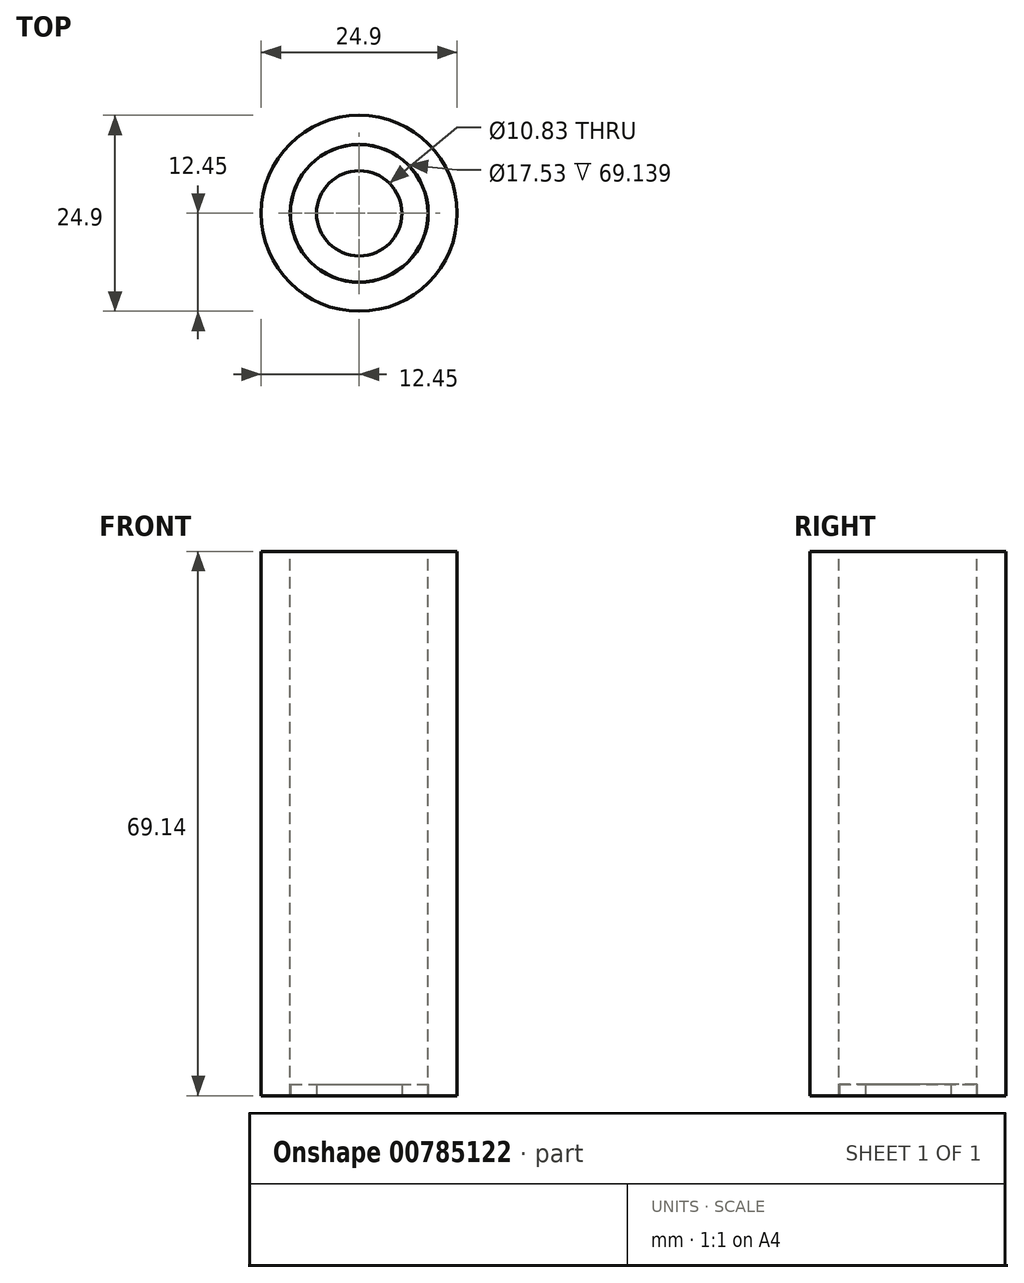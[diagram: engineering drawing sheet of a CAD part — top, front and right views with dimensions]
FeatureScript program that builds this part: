
annotation { "Feature Type Name" : "Feature", "Feature Type Description" : "" }
export const myFeature = defineFeature(function(context is Context, id is Id, definition is map)
    precondition{}
    {
        {
            var Q0;
            Q0=qCreatedBy(makeId("Top.planeOp"),FACE);
            var sketch = newSketch(context, id + "F0", { "sketchPlane" : qUnion([Q0])});
            skCircle(sketch, "E0", {"center": v(0, 0) * mm, "radius": 12.45 * mm});
            skSolve(sketch);
        }
        {
            var Q0;
            Q0=makeQuery(id+"F0.imprint","IMPRINT",FACE,{"disambiguationData":[TD([[makeQuery(id+"F0.imprint","IMPRINT",EDGE,{"derivedFrom":sQuery(id+"F0.wireOp",EDGE,"E0")}),1.0]])]});
            extrude(context, id + "F1", {"entities" : qUnion([Q0]), "depth" : 69.14 * mm, "offsetDistance" : 25.4 * mm});
        }
        {
            var Q0;
            Q0=makeQuery(id+"F1.opExtrude","CAP_FACE",FACE,{"disambiguationData":[OSD([sQuery(id+"F0.wireOp",EDGE,"E0")])],"isStart":false});
            var sketch = newSketch(context, id + "F2", { "sketchPlane" : qUnion([Q0])});
            skSolve(sketch);
        }
        {
            var Q0;
            Q0=makeQuery(id+"F2.imprint","IMPRINT",FACE,{"disambiguationData":[TD([[makeQuery(id+"F2.imprint","IMPRINT",EDGE,{"derivedFrom":makeQuery(id+"F1.opExtrude","CAP_EDGE",EDGE,{"disambiguationData":[OSD([sQuery(id+"F0.wireOp",EDGE,"E0")])],"isStart":false})}),1.0]])]});
            var sketch = newSketch(context, id + "F3", { "sketchPlane" : qUnion([Q0])});
            skCircle(sketch, "E1", {"center": v(0, 0) * mm, "radius": 8.76 * mm});
            skSolve(sketch);
        }
        {
            var Q0;
            Q0 = qSketchRegion(id + "F3", true);
            extrude(context, id + "F4", {"entities" : qUnion([Q0]), "operationType" : NewBodyOperationType.REMOVE, "endBound" : BoundingType.THROUGH_ALL, "oppositeDirection" : true, "depth" : 25.4 * mm, "offsetDistance" : 25.4 * mm});
        }
        {
            var Q0;
            Q0=makeQuery(id+"F1.opExtrude","CAP_FACE",FACE,{"disambiguationData":[OSD([sQuery(id+"F0.wireOp",EDGE,"E0")])],"isStart":true});
            var sketch = newSketch(context, id + "F5", { "sketchPlane" : qUnion([Q0])});
            skCircle(sketch, "E2", {"center": v(0, 0) * mm, "radius": 8.74 * mm});
            skSolve(sketch);
        }
        {
            var Q0;
            Q0=makeQuery(id+"F5.imprint","IMPRINT",FACE,{"disambiguationData":[TD([[makeQuery(id+"F5.imprint","IMPRINT",EDGE,{"derivedFrom":sQuery(id+"F5.wireOp",EDGE,"E2")}),1.0]])]});
            extrude(context, id + "F6", {"entities" : qUnion([Q0]), "oppositeDirection" : true, "depth" : 1.42 * mm, "offsetDistance" : 25.4 * mm});
        }
        {
            var Q0;
            Q0=makeQuery(id+"F6.opExtrude","CAP_FACE",FACE,{"disambiguationData":[OSD([sQuery(id+"F5.wireOp",EDGE,"E2")])],"isStart":true});
            var sketch = newSketch(context, id + "F7", { "sketchPlane" : qUnion([Q0])});
            skCircle(sketch, "E3", {"center": v(0, 0) * mm, "radius": 5.41 * mm});
            skSolve(sketch);
        }
        {
            var Q0;
            Q0=makeQuery(id+"F7.imprint","IMPRINT",FACE,{"disambiguationData":[TD([[makeQuery(id+"F7.imprint","IMPRINT",EDGE,{"derivedFrom":sQuery(id+"F7.wireOp",EDGE,"E3")}),1.0]])]});
            extrude(context, id + "F8", {"entities" : qUnion([Q0]), "operationType" : NewBodyOperationType.ADD, "depth" : 25.4 * mm, "offsetDistance" : 25.4 * mm});
        }
        {
            var Q0;
            Q0=makeQuery(id+"F8.opExtrude","CAP_FACE",FACE,{"disambiguationData":[OSD([sQuery(id+"F7.wireOp",EDGE,"E3")])],"isStart":false});
            extrude(context, id + "F9", {"entities" : qUnion([Q0]), "operationType" : NewBodyOperationType.REMOVE, "endBound" : BoundingType.THROUGH_ALL, "oppositeDirection" : true, "depth" : 25.4 * mm, "offsetDistance" : 25.4 * mm});
        }
    });
